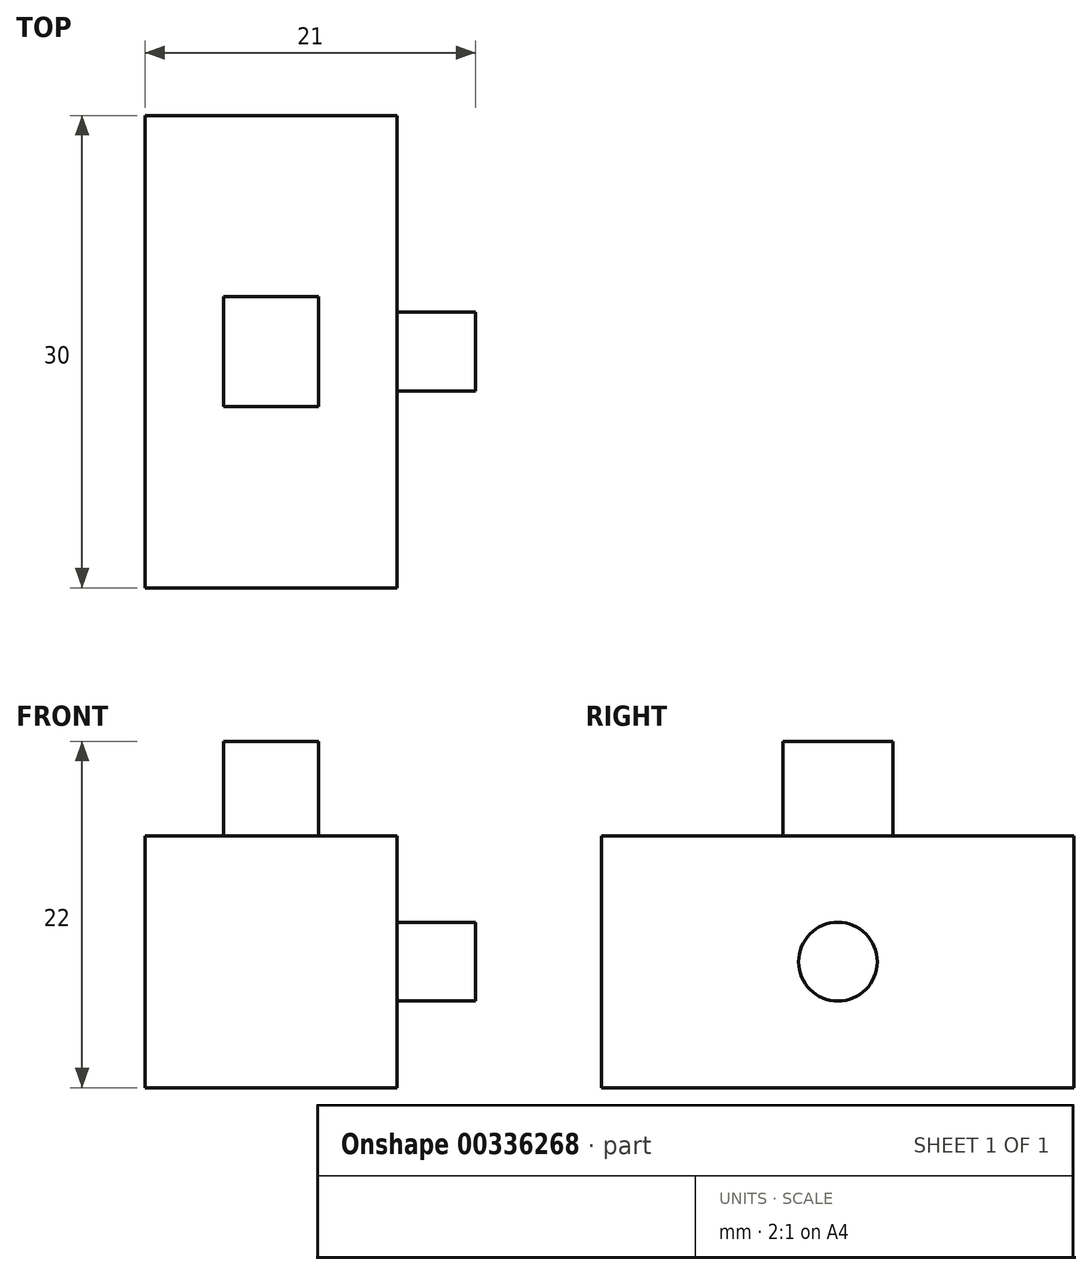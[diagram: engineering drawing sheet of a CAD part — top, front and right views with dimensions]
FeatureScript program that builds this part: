
annotation { "Feature Type Name" : "Feature", "Feature Type Description" : "" }
export const myFeature = defineFeature(function(context is Context, id is Id, definition is map)
    precondition{}
    {
        {
            var Q0;
            Q0=qCreatedBy(makeId("Top.planeOp"),FACE);
            var sketch = newSketch(context, id + "F0", { "sketchPlane" : qUnion([Q0])});
            skLineSegment(sketch, "E0.bottom", {"start": v(0, 0) * mm, "end": v(16, 0) * mm});
            skLineSegment(sketch, "E0.top", {"start": v(0, 30) * mm, "end": v(16, 30) * mm});
            skLineSegment(sketch, "E0.left", {"start": v(0, 0) * mm, "end": v(0, 30) * mm});
            skLineSegment(sketch, "E0.right", {"start": v(16, 0) * mm, "end": v(16, 30) * mm});
            skSolve(sketch);
        }
        {
            var Q0;
            Q0 = qSketchRegion(id + "F0", true);
            extrude(context, id + "F1", {"entities" : qUnion([Q0]), "depth" : 16 * mm});
        }
        {
            var Q0;
            Q0=makeQuery(id+"F1.opExtrude","CAP_FACE",FACE,{"disambiguationData":[OSD([sQuery(id+"F0.wireOp",EDGE,"E0.bottom"),sQuery(id+"F0.wireOp",EDGE,"E0.top"),sQuery(id+"F0.wireOp",EDGE,"E0.left"),sQuery(id+"F0.wireOp",EDGE,"E0.right")])],"isStart":false});
            var sketch = newSketch(context, id + "F2", { "sketchPlane" : qUnion([Q0])});
            skLineSegment(sketch, "E1.bottom", {"start": v(5, 18.5) * mm, "end": v(11, 18.5) * mm});
            skLineSegment(sketch, "E1.top", {"start": v(5, 11.5) * mm, "end": v(11, 11.5) * mm});
            skLineSegment(sketch, "E1.left", {"start": v(5, 18.5) * mm, "end": v(5, 11.5) * mm});
            skLineSegment(sketch, "E1.right", {"start": v(11, 18.5) * mm, "end": v(11, 11.5) * mm});
            skPoint(sketch, "E1.middle", {"position": v(8, 15) * mm});
            skPoint(sketch, "E1.middle.positionSnap0", {"position": v(16, 15) * mm});
            skPoint(sketch, "E1.middle.positionSnap1", {"position": v(8, 30) * mm});
            skPoint(sketch, "E1.centerSnap0", {"position": v(16, 15) * mm});
            skPoint(sketch, "E1.centerSnap1", {"position": v(8, 30) * mm});
            skSolve(sketch);
        }
        {
            var Q0;
            Q0 = qSketchRegion(id + "F2", true);
            extrude(context, id + "F3", {"entities" : qUnion([Q0]), "operationType" : NewBodyOperationType.ADD, "depth" : 6 * mm});
        }
        {
            var Q0;
            Q0=makeQuery(id+"F1.opExtrude","SWEPT_FACE",FACE,{"disambiguationData":[OSD([sQuery(id+"F0.wireOp",EDGE,"E0.right")])]});
            var sketch = newSketch(context, id + "F4", { "sketchPlane" : qUnion([Q0])});
            skCircle(sketch, "E2", {"center": v(15, 8) * mm, "radius": 2.5 * mm});
            skPoint(sketch, "E2.centerSnap0", {"position": v(30, 8) * mm});
            skPoint(sketch, "E2.centerSnap1", {"position": v(15, 16) * mm});
            skSolve(sketch);
        }
        {
            var Q0;
            Q0 = qSketchRegion(id + "F4", true);
            extrude(context, id + "F5", {"entities" : qUnion([Q0]), "operationType" : NewBodyOperationType.ADD, "depth" : 5 * mm});
        }
    });
